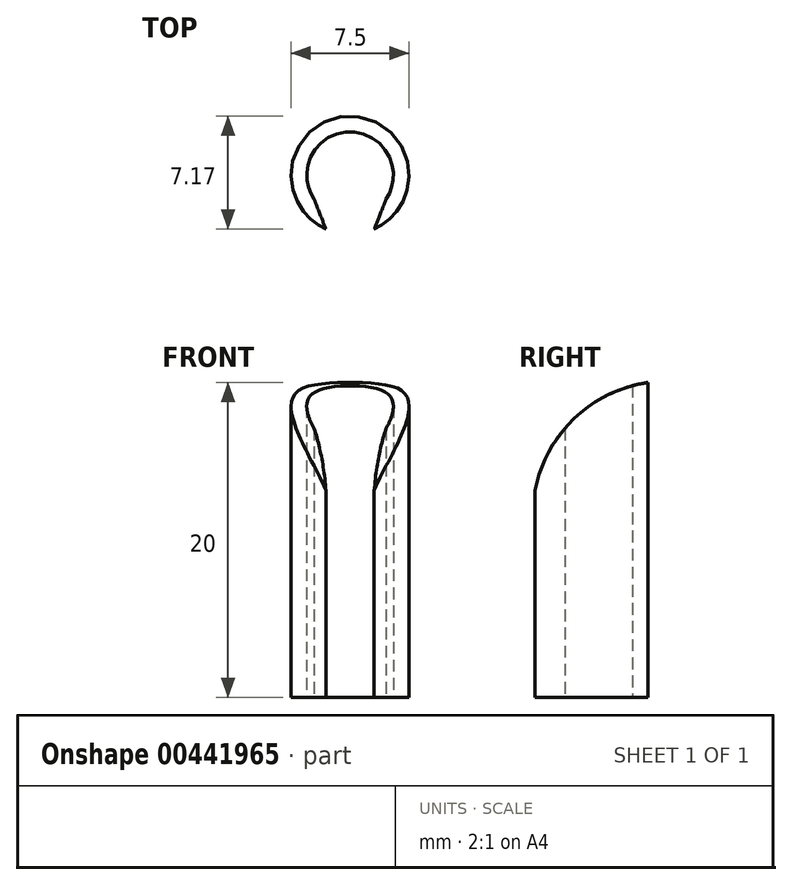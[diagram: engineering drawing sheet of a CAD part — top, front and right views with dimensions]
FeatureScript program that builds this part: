
annotation { "Feature Type Name" : "Feature", "Feature Type Description" : "" }
export const myFeature = defineFeature(function(context is Context, id is Id, definition is map)
    precondition{}
    {
        {
            var Q0;
            Q0=qCreatedBy(makeId("Top.planeOp"),FACE);
            var sketch = newSketch(context, id + "F0", { "sketchPlane" : qUnion([Q0])});
            skCircle(sketch, "E0", {"center": v(0, 0) * mm, "radius": 2.75 * mm});
            skCircle(sketch, "E1", {"center": v(0, 0) * mm, "radius": 3.75 * mm});
            skLineSegment(sketch, "E2", {"start": v(-2.29, -1.53) * mm, "end": v(-1.54, -3.42) * mm});
            skLineSegment(sketch, "E3.MirrorCS", {"start": v(2.29, -1.53) * mm, "end": v(1.54, -3.42) * mm});
            skSolve(sketch);
        }
        {
            var Q0;
            {var subQ0=sQuery(id+"F0.wireOp",EDGE,"E2");Q0=makeQuery(id+"F0.imprint","IMPRINT",FACE,{"disambiguationData":[TD([[makeQuery(id+"F0.imprint","IMPRINT",EDGE,{"derivedFrom":subQ0}),-1.0]])]});}
            extrude(context, id + "F1", {"entities" : qUnion([Q0]), "depth" : 20 * mm, "offsetDistance" : 25.4 * mm});
        }
        {
            var Q0;
            Q0=qCreatedBy(makeId("Right.planeOp"),FACE);
            var sketch = newSketch(context, id + "F2", { "sketchPlane" : qUnion([Q0])});
            skPoint(sketch, "E4", {"position": v(3.75, 0) * mm});
            skPoint(sketch, "E5", {"position": v(-3.45, 0) * mm});
            skLineSegment(sketch, "E6", {"start": v(3.75, 0) * mm, "end": v(3.75, 20) * mm});
            skLineSegment(sketch, "E7", {"start": v(-3.45, 0) * mm, "end": v(-3.45, 20) * mm});
            skArc(sketch, "E8", {"start": v(3.75, 20) * mm, "mid": v(-0.98, 17.66) * mm, "end": v(-3.45, 13) * mm});
            skLineSegment(sketch, "E9", {"start": v(-3.45, 13) * mm, "end": v(-3.45, 20) * mm});
            skLineSegment(sketch, "E10", {"start": v(3.75, 20) * mm, "end": v(-3.45, 20) * mm});
            skSolve(sketch);
        }
        {
            var Q0;
            Q0 = qSketchRegion(id + "F2", true);
            extrude(context, id + "F3", {"entities" : qUnion([Q0]), "operationType" : NewBodyOperationType.REMOVE, "endBound" : BoundingType.SYMMETRIC, "oppositeDirection" : true, "depth" : 25.4 * mm, "offsetDistance" : 25.4 * mm});
        }
    });
